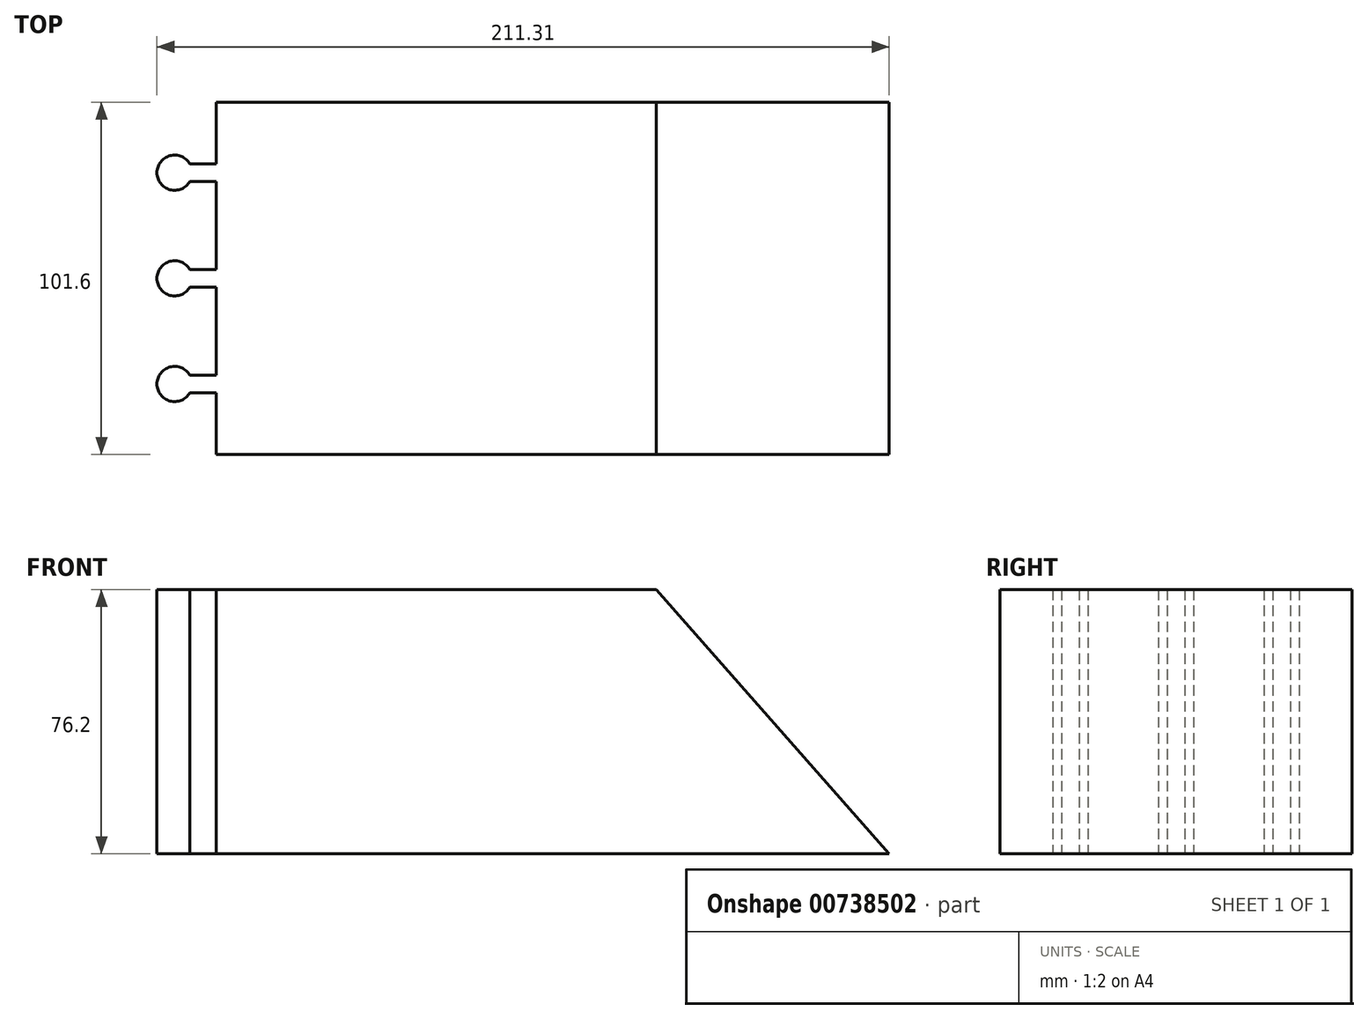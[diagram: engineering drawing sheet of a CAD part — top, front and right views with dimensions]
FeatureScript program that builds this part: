
annotation { "Feature Type Name" : "Feature", "Feature Type Description" : "" }
export const myFeature = defineFeature(function(context is Context, id is Id, definition is map)
    precondition{}
    {
        {
            var Q0;
            Q0=qCreatedBy(makeId("Top.planeOp"),FACE);
            var sketch = newSketch(context, id + "F0", { "sketchPlane" : qUnion([Q0])});
            skLineSegment(sketch, "E0.bottom", {"start": v(-41.28, 35.68) * mm, "end": v(85.72, 35.68) * mm});
            skLineSegment(sketch, "E0.top", {"start": v(-41.28, -65.92) * mm, "end": v(85.72, -65.92) * mm});
            skLineSegment(sketch, "E0.left", {"start": v(-41.28, 35.68) * mm, "end": v(-41.28, -65.92) * mm});
            skLineSegment(sketch, "E0.right", {"start": v(85.72, 35.68) * mm, "end": v(85.72, -65.92) * mm});
            skSolve(sketch);
        }
        {
            var Q0;
            Q0=makeQuery(id+"F0.imprint","IMPRINT",FACE,{"disambiguationData":[TD([[makeQuery(id+"F0.imprint","IMPRINT",EDGE,{"derivedFrom":sQuery(id+"F0.wireOp",EDGE,"E0.bottom")}),-1.0]])]});
            extrude(context, id + "F1", {"entities" : qUnion([Q0]), "depth" : 76.2 * mm, "offsetDistance" : 25.4 * mm});
        }
        {
            var Q0;
            Q0=makeQuery(id+"F1.opExtrude","SWEPT_FACE",FACE,{"disambiguationData":[OSD([sQuery(id+"F0.wireOp",EDGE,"E0.top")])]});
            var sketch = newSketch(context, id + "F2", { "sketchPlane" : qUnion([Q0])});
            skLineSegment(sketch, "E1", {"start": v(85.72, 76.2) * mm, "end": v(152.93, 0) * mm});
            skLineSegment(sketch, "E2", {"start": v(152.93, 0) * mm, "end": v(85.72, 0) * mm});
            skLineSegment(sketch, "E3", {"start": v(85.72, 0) * mm, "end": v(85.72, 76.2) * mm});
            skSolve(sketch);
        }
        {
            var Q0;
            Q0=makeQuery(id+"F2.imprint","IMPRINT",FACE,{"disambiguationData":[TD([[makeQuery(id+"F2.imprint","IMPRINT",EDGE,{"derivedFrom":sQuery(id+"F2.wireOp",EDGE,"E1")}),-1.0]])]});
            extrude(context, id + "F3", {"entities" : qUnion([Q0]), "operationType" : NewBodyOperationType.ADD, "oppositeDirection" : true, "depth" : 101.6 * mm, "offsetDistance" : 25.4 * mm});
        }
        {
            var Q0;
            Q0=makeQuery(id+"F3.boolean.opBoolean","MERGE",FACE,{"derivedFrom":[makeQuery(id+"F1.opExtrude","CAP_FACE",FACE,{"disambiguationData":[OSD([sQuery(id+"F0.wireOp",EDGE,"E0.bottom"),sQuery(id+"F0.wireOp",EDGE,"E0.top"),sQuery(id+"F0.wireOp",EDGE,"E0.left"),sQuery(id+"F0.wireOp",EDGE,"E0.right")])],"isStart":true}),makeQuery(id+"F3.opExtrude","SWEPT_FACE",FACE,{"disambiguationData":[OSD([sQuery(id+"F2.wireOp",EDGE,"E2")])]})]});
            var sketch = newSketch(context, id + "F4", { "sketchPlane" : qUnion([Q0])});
            skLineSegment(sketch, "E4.bottom", {"start": v(-41.28, -17.9) * mm, "end": v(-48.9, -17.9) * mm});
            skLineSegment(sketch, "E4.top", {"start": v(-41.28, -12.82) * mm, "end": v(-48.9, -12.82) * mm});
            skLineSegment(sketch, "E4.left", {"start": v(-41.28, -17.9) * mm, "end": v(-41.28, -12.82) * mm});
            skLineSegment(sketch, "E4.right", {"start": v(-48.9, -17.9) * mm, "end": v(-48.9, -12.82) * mm});
            skLineSegment(sketch, "E5.bottom", {"start": v(-41.28, 12.58) * mm, "end": v(-48.9, 12.58) * mm});
            skLineSegment(sketch, "E5.top", {"start": v(-41.28, 17.66) * mm, "end": v(-48.9, 17.66) * mm});
            skLineSegment(sketch, "E5.left", {"start": v(-41.28, 12.58) * mm, "end": v(-41.28, 17.66) * mm});
            skLineSegment(sketch, "E5.right", {"start": v(-48.9, 12.58) * mm, "end": v(-48.9, 17.66) * mm});
            skLineSegment(sketch, "E6.bottom", {"start": v(-41.28, 43.06) * mm, "end": v(-48.9, 43.06) * mm});
            skLineSegment(sketch, "E6.top", {"start": v(-41.28, 48.14) * mm, "end": v(-48.9, 48.14) * mm});
            skLineSegment(sketch, "E6.left", {"start": v(-41.28, 43.06) * mm, "end": v(-41.28, 48.14) * mm});
            skLineSegment(sketch, "E6.right", {"start": v(-48.9, 43.06) * mm, "end": v(-48.9, 48.14) * mm});
            skArc(sketch, "E7", {"start": v(-48.9, -12.82) * mm, "mid": v(-58.38, -15.36) * mm, "end": v(-48.9, -17.9) * mm});
            skArc(sketch, "E8", {"start": v(-48.9, 17.66) * mm, "mid": v(-58.38, 15.12) * mm, "end": v(-48.9, 12.58) * mm});
            skArc(sketch, "E9", {"start": v(-48.9, 48.14) * mm, "mid": v(-58.38, 45.6) * mm, "end": v(-48.9, 43.06) * mm});
            skSolve(sketch);
        }
        {
            var Q0;
            Q0=makeQuery(id+"F4.imprint","IMPRINT",FACE,{"disambiguationData":[TD([[makeQuery(id+"F4.imprint","IMPRINT",EDGE,{"derivedFrom":sQuery(id+"F4.wireOp",EDGE,"E4.bottom")}),-1.0]])]});
            var Q1;
            Q1=makeQuery(id+"F4.imprint","IMPRINT",FACE,{"disambiguationData":[TD([[makeQuery(id+"F4.imprint","IMPRINT",EDGE,{"derivedFrom":sQuery(id+"F4.wireOp",EDGE,"E6.right")}),1.0]])]});
            var Q2;
            Q2=makeQuery(id+"F4.imprint","IMPRINT",FACE,{"disambiguationData":[TD([[makeQuery(id+"F4.imprint","IMPRINT",EDGE,{"derivedFrom":sQuery(id+"F4.wireOp",EDGE,"E6.bottom")}),-1.0]])]});
            var Q3;
            Q3=makeQuery(id+"F4.imprint","IMPRINT",FACE,{"disambiguationData":[TD([[makeQuery(id+"F4.imprint","IMPRINT",EDGE,{"derivedFrom":sQuery(id+"F4.wireOp",EDGE,"E5.right")}),1.0]])]});
            var Q4;
            Q4=makeQuery(id+"F4.imprint","IMPRINT",FACE,{"disambiguationData":[TD([[makeQuery(id+"F4.imprint","IMPRINT",EDGE,{"derivedFrom":sQuery(id+"F4.wireOp",EDGE,"E5.bottom")}),-1.0]])]});
            var Q5;
            Q5=makeQuery(id+"F4.imprint","IMPRINT",FACE,{"disambiguationData":[TD([[makeQuery(id+"F4.imprint","IMPRINT",EDGE,{"derivedFrom":sQuery(id+"F4.wireOp",EDGE,"E4.right")}),1.0]])]});
            extrude(context, id + "F5", {"entities" : qUnion([Q0, Q1, Q2, Q3, Q4, Q5]), "operationType" : NewBodyOperationType.ADD, "oppositeDirection" : true, "depth" : 76.2 * mm, "offsetDistance" : 25.4 * mm});
        }
    });
